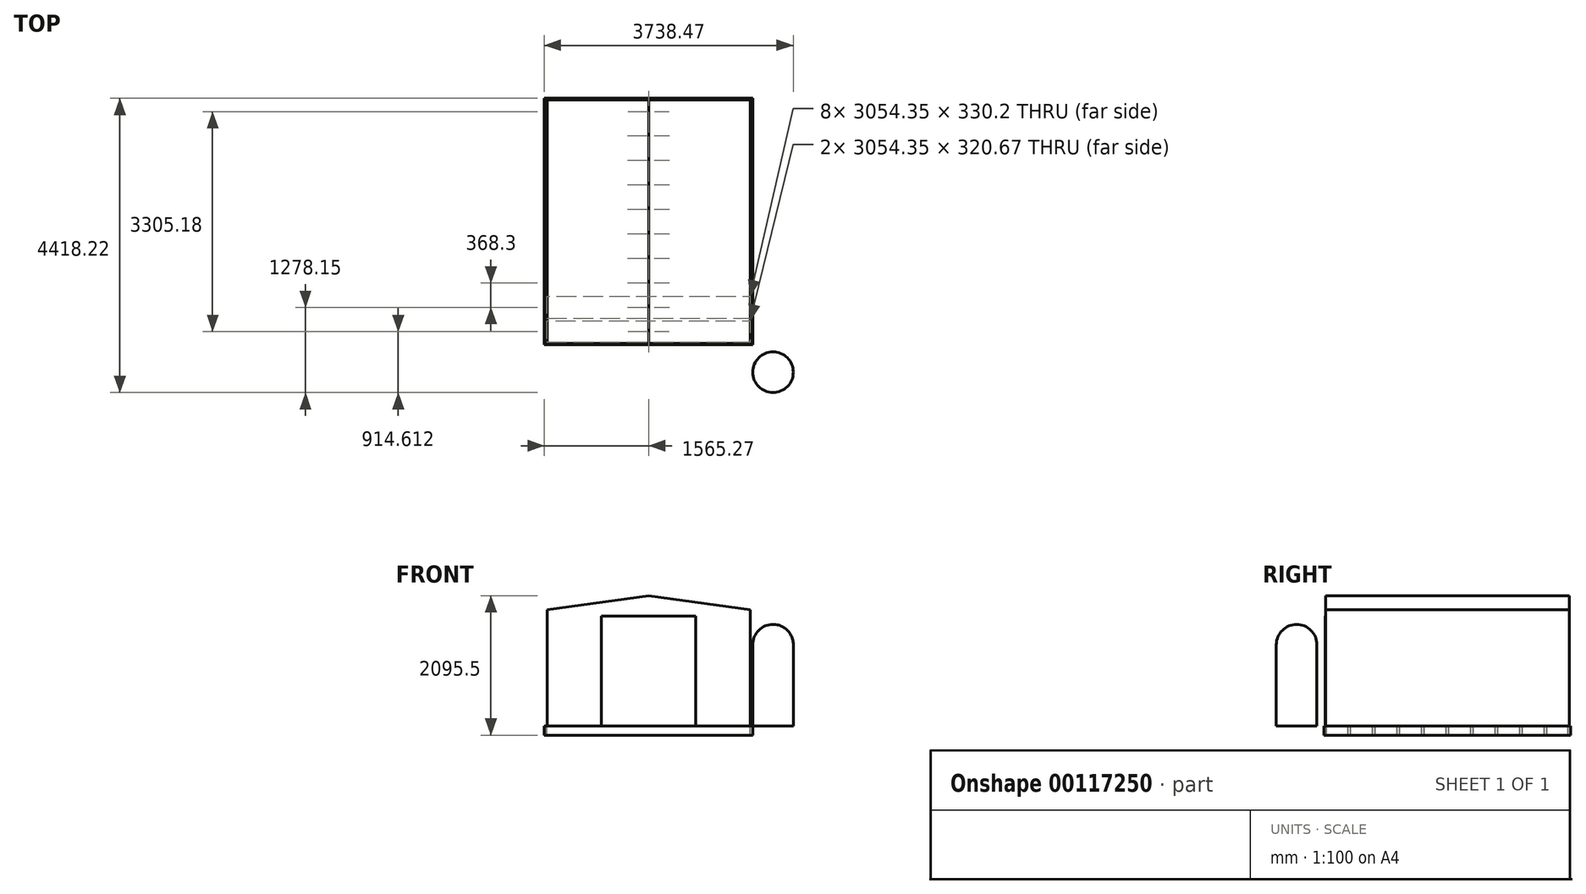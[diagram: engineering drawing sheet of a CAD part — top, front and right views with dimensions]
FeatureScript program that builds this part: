
annotation { "Feature Type Name" : "Feature", "Feature Type Description" : "" }
export const myFeature = defineFeature(function(context is Context, id is Id, definition is map)
    precondition{}
    {
        {
            var Q0;
            Q0=qCreatedBy(makeId("Top.planeOp"),FACE);
            var sketch = newSketch(context, id + "F0", { "sketchPlane" : qUnion([Q0])});
            skLineSegment(sketch, "E0.bottom", {"start": v(1565.28, -1851.02) * mm, "end": v(-1565.27, -1851.02) * mm});
            skLineSegment(sketch, "E0.top", {"start": v(1565.28, 1851.02) * mm, "end": v(-1565.27, 1851.02) * mm});
            skLineSegment(sketch, "E0.left", {"start": v(1565.27, -1851.02) * mm, "end": v(1565.27, 1851.02) * mm});
            skLineSegment(sketch, "E0.right", {"start": v(-1565.28, -1851.02) * mm, "end": v(-1565.28, 1851.02) * mm});
            skPoint(sketch, "E0.middle", {"position": v(0, 0) * mm});
            skLineSegment(sketch, "E1.bottom", {"start": v(1527.18, -1812.92) * mm, "end": v(-1527.17, -1812.92) * mm});
            skLineSegment(sketch, "E1.top", {"start": v(1527.18, 1812.92) * mm, "end": v(-1527.17, 1812.92) * mm});
            skLineSegment(sketch, "E1.left", {"start": v(1527.18, -1812.92) * mm, "end": v(1527.18, 1812.93) * mm});
            skLineSegment(sketch, "E1.right", {"start": v(-1527.18, -1812.92) * mm, "end": v(-1527.18, 1812.92) * mm});
            skLineSegment(sketch, "E2", {"start": v(-1813.6, 0) * mm, "end": v(2095.33, 0) * mm, "construction": true});
            skPoint(sketch, "E2.endSnap0", {"position": v(-1565.28, 0) * mm});
            skLineSegment(sketch, "E3.bottom", {"start": v(1527.18, -19.05) * mm, "end": v(-1527.18, -19.05) * mm});
            skLineSegment(sketch, "E3.top", {"start": v(1527.18, 19.05) * mm, "end": v(-1527.18, 19.05) * mm});
            skLineSegment(sketch, "E3.left", {"start": v(1527.18, -19.05) * mm, "end": v(1527.18, 19.05) * mm});
            skLineSegment(sketch, "E3.right", {"start": v(-1527.18, -19.05) * mm, "end": v(-1527.18, 19.05) * mm});
            skLineSegment(sketch, "E4.bottom", {"start": v(1527.17, 349.25) * mm, "end": v(-1527.18, 349.25) * mm});
            skLineSegment(sketch, "E4.top", {"start": v(1527.18, 387.35) * mm, "end": v(-1527.17, 387.35) * mm});
            skLineSegment(sketch, "E4.left", {"start": v(1527.18, 349.25) * mm, "end": v(1527.18, 387.35) * mm});
            skLineSegment(sketch, "E4.right", {"start": v(-1527.18, 349.25) * mm, "end": v(-1527.18, 387.35) * mm});
            skPoint(sketch, "E4.middle", {"position": v(0, 368.3) * mm});
            skPoint(sketch, "E4.middle.positionSnap0", {"position": v(0, 19.05) * mm});
            skPoint(sketch, "E4.centerSnap0", {"position": v(0, 19.05) * mm});
            skLineSegment(sketch, "E5.bottom", {"start": v(1527.18, 717.55) * mm, "end": v(-1527.18, 717.55) * mm});
            skLineSegment(sketch, "E5.top", {"start": v(1527.18, 755.65) * mm, "end": v(-1527.18, 755.65) * mm});
            skLineSegment(sketch, "E5.left", {"start": v(1527.18, 717.55) * mm, "end": v(1527.18, 755.65) * mm});
            skLineSegment(sketch, "E5.right", {"start": v(-1527.18, 717.55) * mm, "end": v(-1527.18, 755.65) * mm});
            skPoint(sketch, "E5.middle", {"position": v(0, 736.6) * mm});
            skLineSegment(sketch, "E6.bottom", {"start": v(1527.17, 1085.85) * mm, "end": v(-1527.17, 1085.85) * mm});
            skLineSegment(sketch, "E6.top", {"start": v(1527.18, 1123.95) * mm, "end": v(-1527.18, 1123.95) * mm});
            skLineSegment(sketch, "E6.left", {"start": v(1527.18, 1085.85) * mm, "end": v(1527.18, 1123.95) * mm});
            skLineSegment(sketch, "E6.right", {"start": v(-1527.18, 1085.85) * mm, "end": v(-1527.18, 1123.95) * mm});
            skPoint(sketch, "E6.middle", {"position": v(0, 1104.9) * mm});
            skLineSegment(sketch, "E7.bottom", {"start": v(1527.18, 1454.15) * mm, "end": v(-1527.18, 1454.15) * mm});
            skLineSegment(sketch, "E7.top", {"start": v(1527.18, 1492.25) * mm, "end": v(-1527.17, 1492.25) * mm});
            skLineSegment(sketch, "E7.left", {"start": v(1527.18, 1454.15) * mm, "end": v(1527.18, 1492.25) * mm});
            skLineSegment(sketch, "E7.right", {"start": v(-1527.18, 1454.15) * mm, "end": v(-1527.18, 1492.25) * mm});
            skPoint(sketch, "E7.middle", {"position": v(0, 1473.2) * mm});
            skPoint(sketch, "E7.middle.positionSnap0", {"position": v(0, 1123.95) * mm});
            skPoint(sketch, "E7.centerSnap0", {"position": v(0, 1123.95) * mm});
            skLineSegment(sketch, "E8.MirrorCS", {"start": v(-1527.18, 19.05) * mm, "end": v(-1527.18, -19.05) * mm});
            skLineSegment(sketch, "E9.MirrorCS", {"start": v(1527.18, -717.55) * mm, "end": v(1527.18, -755.65) * mm});
            skLineSegment(sketch, "E10.MirrorCS", {"start": v(1527.18, -349.25) * mm, "end": v(1527.18, -387.35) * mm});
            skLineSegment(sketch, "E11.MirrorCS", {"start": v(-1527.18, -1454.15) * mm, "end": v(-1527.18, -1492.25) * mm});
            skPoint(sketch, "E12.MirrorP", {"position": v(0, -1123.95) * mm});
            skLineSegment(sketch, "E13.MirrorCS", {"start": v(-1527.18, -1085.85) * mm, "end": v(-1527.18, -1123.95) * mm});
            skLineSegment(sketch, "E14.MirrorCS", {"start": v(-1527.18, -349.25) * mm, "end": v(-1527.18, -387.35) * mm});
            skLineSegment(sketch, "E15.MirrorCS", {"start": v(-1527.18, -717.55) * mm, "end": v(-1527.18, -755.65) * mm});
            skLineSegment(sketch, "E16.MirrorCS", {"start": v(1527.18, -1085.85) * mm, "end": v(1527.18, -1123.95) * mm});
            skLineSegment(sketch, "E17.MirrorCS", {"start": v(1527.18, -1454.15) * mm, "end": v(1527.18, -1492.25) * mm});
            skLineSegment(sketch, "E18.MirrorCS", {"start": v(1527.18, 19.05) * mm, "end": v(1527.18, -19.05) * mm});
            skPoint(sketch, "E19.MirrorP", {"position": v(0, -19.05) * mm});
            skPoint(sketch, "E20.MirrorP", {"position": v(0, -1473.2) * mm});
            skLineSegment(sketch, "E21.MirrorCS", {"start": v(1527.18, -1492.25) * mm, "end": v(-1527.17, -1492.25) * mm});
            skLineSegment(sketch, "E22.MirrorCS", {"start": v(1527.17, -349.25) * mm, "end": v(-1527.18, -349.25) * mm});
            skLineSegment(sketch, "E23.MirrorCS", {"start": v(1527.18, -387.35) * mm, "end": v(-1527.17, -387.35) * mm});
            skPoint(sketch, "E24.MirrorP", {"position": v(0, -736.6) * mm});
            skLineSegment(sketch, "E25.MirrorCS", {"start": v(1527.18, -755.65) * mm, "end": v(-1527.18, -755.65) * mm});
            skPoint(sketch, "E26.MirrorP", {"position": v(0, -368.3) * mm});
            skLineSegment(sketch, "E27.MirrorCS", {"start": v(1527.18, -1123.95) * mm, "end": v(-1527.18, -1123.95) * mm});
            skLineSegment(sketch, "E28.MirrorCS", {"start": v(1527.17, -1085.85) * mm, "end": v(-1527.17, -1085.85) * mm});
            skLineSegment(sketch, "E29.MirrorCS", {"start": v(1527.18, -717.55) * mm, "end": v(-1527.18, -717.55) * mm});
            skLineSegment(sketch, "E30.MirrorCS", {"start": v(1527.18, -1454.15) * mm, "end": v(-1527.18, -1454.15) * mm});
            skLineSegment(sketch, "E31.MirrorCS", {"start": v(-1527.18, 1812.92) * mm, "end": v(-1527.18, -1812.92) * mm});
            skLineSegment(sketch, "E32.MirrorCS", {"start": v(1527.18, 1812.92) * mm, "end": v(1527.18, -1812.93) * mm});
            skLineSegment(sketch, "E33.MirrorCS", {"start": v(1565.27, 1851.02) * mm, "end": v(1565.27, -1851.02) * mm});
            skLineSegment(sketch, "E34.MirrorCS", {"start": v(-1565.28, 1851.02) * mm, "end": v(-1565.28, -1851.02) * mm});
            skPoint(sketch, "E35.MirrorP", {"position": v(0, -1104.9) * mm});
            skSolve(sketch);
        }
        {
            var Q0;
            Q0 = qSketchRegion(id + "F0", true);
            var Q1;
            {var subQ0=sQuery(id+"F0.wireOp",EDGE,"E22.MirrorCS");Q1=makeQuery(id+"F0.imprint","IMPRINT",FACE,{"disambiguationData":[TD([[makeQuery(id+"F0.imprint","IMPRINT",EDGE,{"derivedFrom":subQ0}),1.0]])]});}
            var Q2;
            {var subQ0=sQuery(id+"F0.wireOp",EDGE,"E25.MirrorCS");Q2=makeQuery(id+"F0.imprint","IMPRINT",FACE,{"disambiguationData":[TD([[makeQuery(id+"F0.imprint","IMPRINT",EDGE,{"derivedFrom":subQ0}),-1.0]])]});}
            var Q3;
            {var subQ0=sQuery(id+"F0.wireOp",EDGE,"E27.MirrorCS");Q3=makeQuery(id+"F0.imprint","IMPRINT",FACE,{"disambiguationData":[TD([[makeQuery(id+"F0.imprint","IMPRINT",EDGE,{"derivedFrom":subQ0}),-1.0]])]});}
            var Q4;
            {var subQ0=sQuery(id+"F0.wireOp",EDGE,"E21.MirrorCS");Q4=makeQuery(id+"F0.imprint","IMPRINT",FACE,{"disambiguationData":[TD([[makeQuery(id+"F0.imprint","IMPRINT",EDGE,{"derivedFrom":subQ0}),-1.0]])]});}
            var Q5;
            {var subQ0=sQuery(id+"F0.wireOp",EDGE,"E3.top");Q5=makeQuery(id+"F0.imprint","IMPRINT",FACE,{"disambiguationData":[TD([[makeQuery(id+"F0.imprint","IMPRINT",EDGE,{"derivedFrom":subQ0}),1.0]])]});}
            var Q6;
            {var subQ0=sQuery(id+"F0.wireOp",EDGE,"E4.bottom");Q6=makeQuery(id+"F0.imprint","IMPRINT",FACE,{"disambiguationData":[TD([[makeQuery(id+"F0.imprint","IMPRINT",EDGE,{"derivedFrom":subQ0}),-1.0]])]});}
            var Q7;
            {var subQ0=sQuery(id+"F0.wireOp",EDGE,"E5.bottom");Q7=makeQuery(id+"F0.imprint","IMPRINT",FACE,{"disambiguationData":[TD([[makeQuery(id+"F0.imprint","IMPRINT",EDGE,{"derivedFrom":subQ0}),-1.0]])]});}
            var Q8;
            {var subQ0=sQuery(id+"F0.wireOp",EDGE,"E6.bottom");Q8=makeQuery(id+"F0.imprint","IMPRINT",FACE,{"disambiguationData":[TD([[makeQuery(id+"F0.imprint","IMPRINT",EDGE,{"derivedFrom":subQ0}),-1.0]])]});}
            var Q9;
            {var subQ0=sQuery(id+"F0.wireOp",EDGE,"E7.bottom");Q9=makeQuery(id+"F0.imprint","IMPRINT",FACE,{"disambiguationData":[TD([[makeQuery(id+"F0.imprint","IMPRINT",EDGE,{"derivedFrom":subQ0}),-1.0]])]});}
            extrude(context, id + "F1", {"entities" : qUnion([Q0, Q1, Q2, Q3, Q4, Q5, Q6, Q7, Q8, Q9]), "oppositeDirection" : true, "depth" : 139.7 * mm});
        }
        {
            var Q0;
            Q0=qCreatedBy(makeId("Top.planeOp"),FACE);
            var sketch = newSketch(context, id + "F2", { "sketchPlane" : qUnion([Q0])});
            skLineSegment(sketch, "E36.bottom", {"start": v(1524, -1828.8) * mm, "end": v(-1524, -1828.8) * mm});
            skLineSegment(sketch, "E36.top", {"start": v(1524, 1828.8) * mm, "end": v(-1524, 1828.8) * mm});
            skLineSegment(sketch, "E36.left", {"start": v(1524, -1828.8) * mm, "end": v(1524, 1828.8) * mm});
            skLineSegment(sketch, "E36.right", {"start": v(-1524, -1828.8) * mm, "end": v(-1524, 1828.8) * mm});
            skPoint(sketch, "E36.middle", {"position": v(0, 0) * mm});
            skSolve(sketch);
        }
        {
            var Q0;
            Q0 = qSketchRegion(id + "F2", true);
            extrude(context, id + "F3", {"entities" : qUnion([Q0]), "depth" : 1955.8 * mm});
        }
        {
            var Q0;
            Q0=makeQuery(id+"F3.opExtrude","CAP_EDGE",EDGE,{"disambiguationData":[OSD([sQuery(id+"F2.wireOp",EDGE,"E36.left")])],"isStart":false});
            var Q1;
            Q1=makeQuery(id+"F3.opExtrude","CAP_EDGE",EDGE,{"disambiguationData":[OSD([sQuery(id+"F2.wireOp",EDGE,"E36.right")])],"isStart":false});
            chamfer(context, id + "F4", {"entities" : qUnion([Q0, Q1]), "chamferType" : ChamferType.OFFSET_ANGLE, "width" : 1524 * mm, "oppositeDirection" : false, "angle" : 8 * degree, "tangentPropagation" : true});
        }
        {
            var Q0;
            Q0=makeQuery(id+"F3.opExtrude","SWEPT_FACE",FACE,{"disambiguationData":[OSD([sQuery(id+"F2.wireOp",EDGE,"E36.bottom")])]});
            var sketch = newSketch(context, id + "F5", { "sketchPlane" : qUnion([Q0])});
            skLineSegment(sketch, "E37.bottom", {"start": v(704.85, 0) * mm, "end": v(-704.85, 0) * mm});
            skLineSegment(sketch, "E37.top", {"start": v(704.85, 1651) * mm, "end": v(-704.85, 1651) * mm});
            skLineSegment(sketch, "E37.left", {"start": v(704.85, 0) * mm, "end": v(704.85, 1651) * mm});
            skLineSegment(sketch, "E37.right", {"start": v(-704.85, 0) * mm, "end": v(-704.85, 1651) * mm});
            skPoint(sketch, "E37.middle", {"position": v(0, 825.5) * mm});
            skPoint(sketch, "E37.middle.positionSnap0", {"position": v(0, 0) * mm});
            skPoint(sketch, "E37.centerSnap0", {"position": v(0, 0) * mm});
            skSolve(sketch);
        }
        {
            var Q0;
            Q0=makeQuery(id+"F5.imprint","IMPRINT",FACE,{"disambiguationData":[TD([[makeQuery(id+"F5.imprint","IMPRINT",EDGE,{"derivedFrom":sQuery(id+"F5.wireOp",EDGE,"E37.bottom")}),-1.0]])]});
            extrude(context, id + "F6", {"entities" : qUnion([Q0]), "depth" : 6.35 * mm});
        }
        {
            var Q0;
            Q0=qCreatedBy(makeId("Top.planeOp"),FACE);
            var sketch = newSketch(context, id + "F7", { "sketchPlane" : qUnion([Q0])});
            skCircle(sketch, "E38", {"center": v(1868.4, -2262.4) * mm, "radius": 304.8 * mm});
            skSolve(sketch);
        }
        {
            var Q0;
            Q0=makeQuery(id+"F7.imprint","IMPRINT",FACE,{"disambiguationData":[TD([[makeQuery(id+"F7.imprint","IMPRINT",EDGE,{"derivedFrom":sQuery(id+"F7.wireOp",EDGE,"E38")}),1.0]])]});
            extrude(context, id + "F8", {"entities" : qUnion([Q0]), "depth" : 1524 * mm});
        }
        {
            var Q0;
            Q0=makeQuery(id+"F8.opExtrude","CAP_EDGE",EDGE,{"disambiguationData":[OSD([sQuery(id+"F7.wireOp",EDGE,"E38")])],"isStart":false});
            fillet(context, id + "F9", {"entities" : qUnion([Q0]), "radius" : 304.8 * mm, "tangentPropagation" : true, "allowEdgeOverflow" : false});
        }
    });
